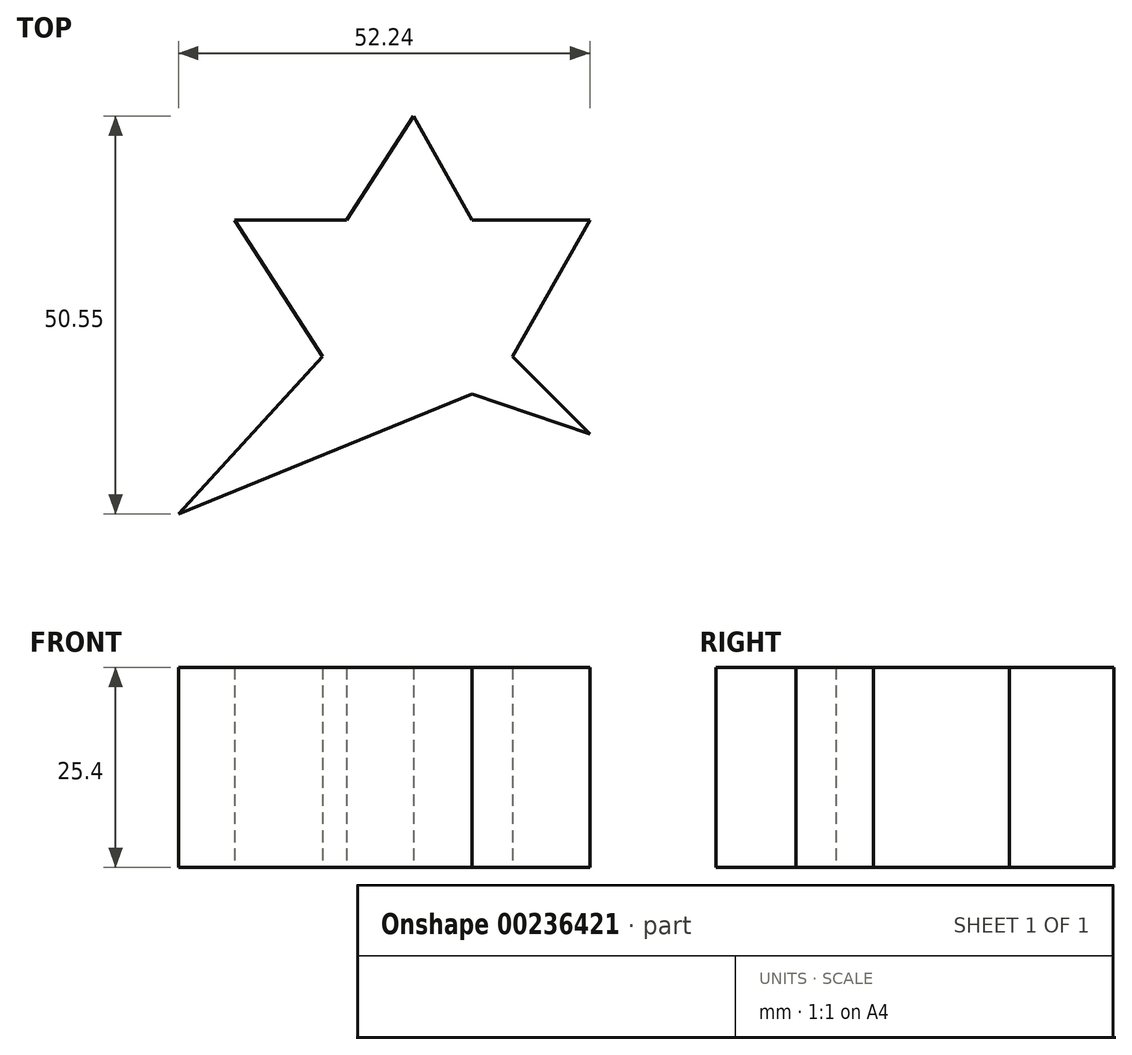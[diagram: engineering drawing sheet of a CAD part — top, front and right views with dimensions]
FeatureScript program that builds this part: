
annotation { "Feature Type Name" : "Feature", "Feature Type Description" : "" }
export const myFeature = defineFeature(function(context is Context, id is Id, definition is map)
    precondition{}
    {
        {
            var Q0;
            Q0=qCreatedBy(makeId("Top.planeOp"),FACE);
            var sketch = newSketch(context, id + "F0", { "sketchPlane" : qUnion([Q0])});
            skLineSegment(sketch, "E0", {"start": v(-41.93, 27.68) * mm, "end": v(-53.12, 44.98) * mm});
            skLineSegment(sketch, "E1", {"start": v(-53.12, 44.98) * mm, "end": v(-38.87, 44.98) * mm});
            skLineSegment(sketch, "E2", {"start": v(-38.87, 44.98) * mm, "end": v(-30.4, 58.2) * mm});
            skLineSegment(sketch, "E3", {"start": v(-30.4, 58.2) * mm, "end": v(-22.93, 44.98) * mm});
            skLineSegment(sketch, "E4", {"start": v(-22.93, 44.98) * mm, "end": v(-8, 44.98) * mm});
            skLineSegment(sketch, "E5", {"start": v(-8, 44.98) * mm, "end": v(-17.84, 27.68) * mm});
            skLineSegment(sketch, "E6", {"start": v(-17.84, 27.68) * mm, "end": v(-8, 17.84) * mm});
            skLineSegment(sketch, "E7", {"start": v(-8, 17.84) * mm, "end": v(-22.93, 22.93) * mm});
            skLineSegment(sketch, "E8", {"start": v(-22.93, 22.93) * mm, "end": v(-60.24, 7.66) * mm});
            skLineSegment(sketch, "E9", {"start": v(-60.24, 7.66) * mm, "end": v(-41.93, 27.68) * mm});
            skSolve(sketch);
        }
        {
            var Q0;
            Q0=makeQuery(id+"F0.imprint","IMPRINT",FACE,{"disambiguationData":[TD([[makeQuery(id+"F0.imprint","IMPRINT",EDGE,{"derivedFrom":sQuery(id+"F0.wireOp",EDGE,"E0")}),-1.0]])]});
            extrude(context, id + "F1", {"entities" : qUnion([Q0]), "depth" : 25.4 * mm});
        }
    });
